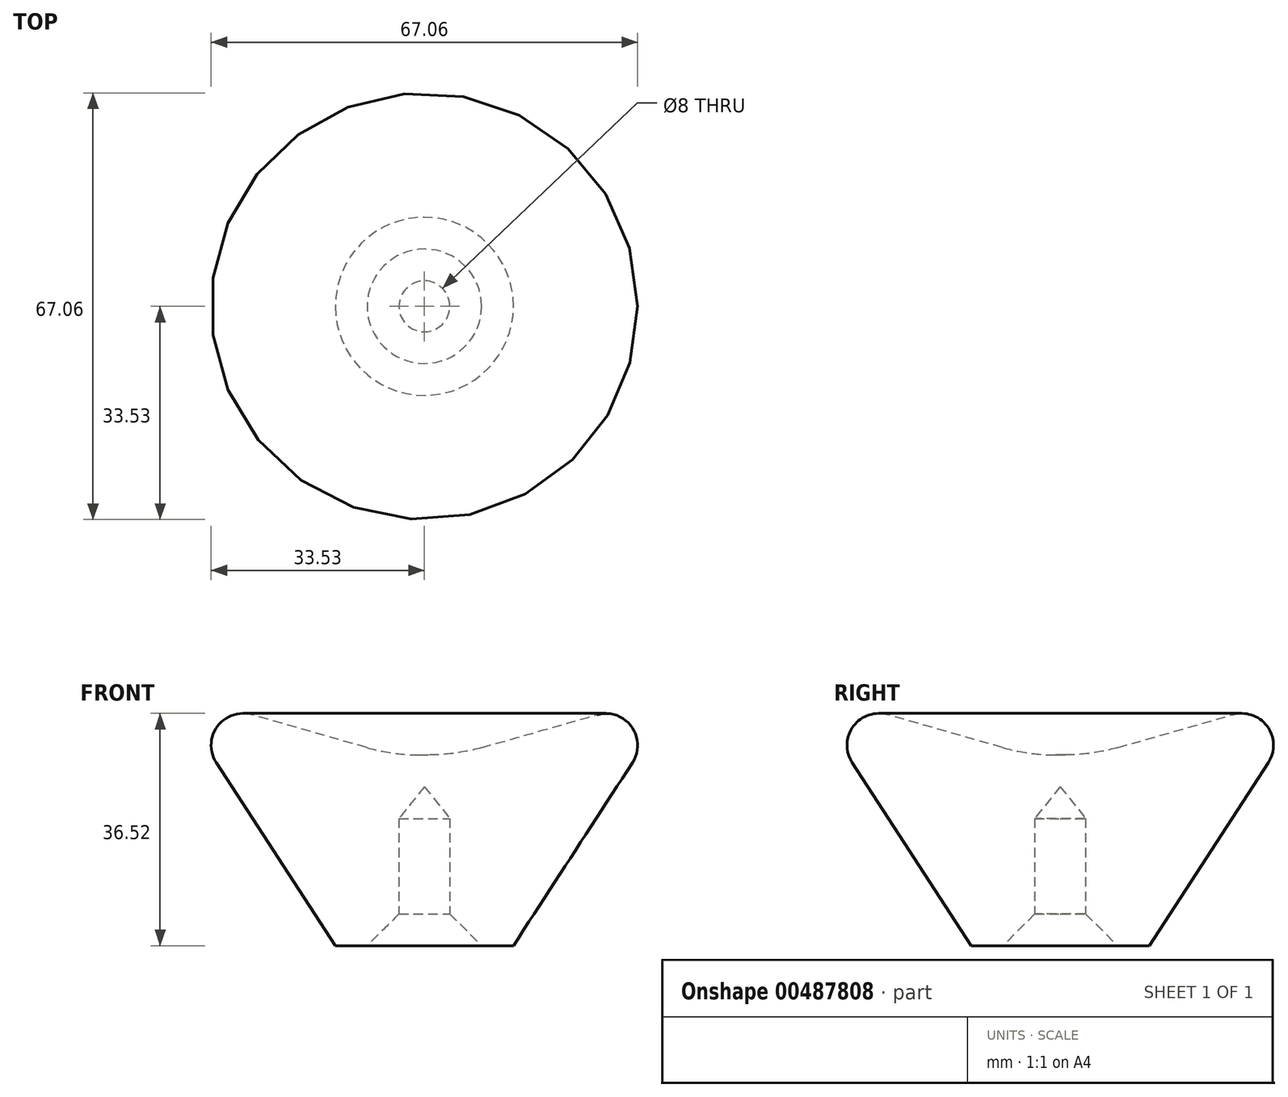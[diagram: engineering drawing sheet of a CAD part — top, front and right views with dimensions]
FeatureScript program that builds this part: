
annotation { "Feature Type Name" : "Feature", "Feature Type Description" : "" }
export const myFeature = defineFeature(function(context is Context, id is Id, definition is map)
    precondition{}
    {
        {
            var Q0;
            Q0=qCreatedBy(makeId("Front.planeOp"),FACE);
            var sketch = newSketch(context, id + "F0", { "sketchPlane" : qUnion([Q0])});
            skLineSegment(sketch, "E0", {"start": v(0, 0) * mm, "end": v(0, 45.38) * mm, "construction": true});
            skLineSegment(sketch, "E1", {"start": v(4, 0) * mm, "end": v(4, 20) * mm});
            skLineSegment(sketch, "E2", {"start": v(4, 20) * mm, "end": v(0, 25) * mm});
            skLineSegment(sketch, "E3", {"start": v(4, 0) * mm, "end": v(14, 0) * mm});
            skLineSegment(sketch, "E4", {"start": v(14, 0) * mm, "end": v(40, 40) * mm});
            skLineSegment(sketch, "E5", {"start": v(0, 30) * mm, "end": v(0, 25) * mm});
            skLineSegment(sketch, "E6", {"start": v(0, 30) * mm, "end": v(5, 30) * mm});
            skLineSegment(sketch, "E7", {"start": v(5, 30) * mm, "end": v(40, 40) * mm});
            skSolve(sketch);
        }
        {
            var Q0;
            Q0=makeQuery(id+"F0.imprint","IMPRINT",FACE,{"disambiguationData":[TD([[makeQuery(id+"F0.imprint","IMPRINT",EDGE,{"derivedFrom":sQuery(id+"F0.wireOp",EDGE,"E1")}),-1.0]])]});
            var Q1;
            Q1=sQuery(id+"F0.wireOp",EDGE,"E0");
            revolve(context, id + "F1", {"surfaceOperationType" : NewSurfaceOperationType.NEW, "entities" : qUnion([Q0]), "axis" : qUnion([Q1]), "revolveType" : RevolveType.FULL});
        }
        {
            var Q0;
            Q0=makeQuery(id+"F1.opRevolve","SWEPT_EDGE",EDGE,{"disambiguationData":[OSD([sQuery(id+"F0.wireOp",EDGE,"E4"),sQuery(id+"F0.wireOp",EDGE,"E7")])]});
            fillet(context, id + "F2", {"entities" : qUnion([Q0]), "radius" : 5 * mm, "tangentPropagation" : true, "allowEdgeOverflow" : false});
        }
        {
            var Q0;
            Q0=makeQuery(id+"F1.opRevolve","SWEPT_EDGE",EDGE,{"disambiguationData":[OSD([sQuery(id+"F0.wireOp",EDGE,"E6"),sQuery(id+"F0.wireOp",EDGE,"E7")])]});
            fillet(context, id + "F3", {"entities" : qUnion([Q0]), "radius" : 30 * mm, "tangentPropagation" : true, "allowEdgeOverflow" : false});
        }
        {
            var Q0;
            Q0=makeQuery(id+"F1.opRevolve","SWEPT_EDGE",EDGE,{"disambiguationData":[OSD([sQuery(id+"F0.wireOp",EDGE,"E1"),sQuery(id+"F0.wireOp",EDGE,"E3")])]});
            chamfer(context, id + "F4", {"entities" : qUnion([Q0]), "width" : 5 * mm, "tangentPropagation" : true});
        }
    });
